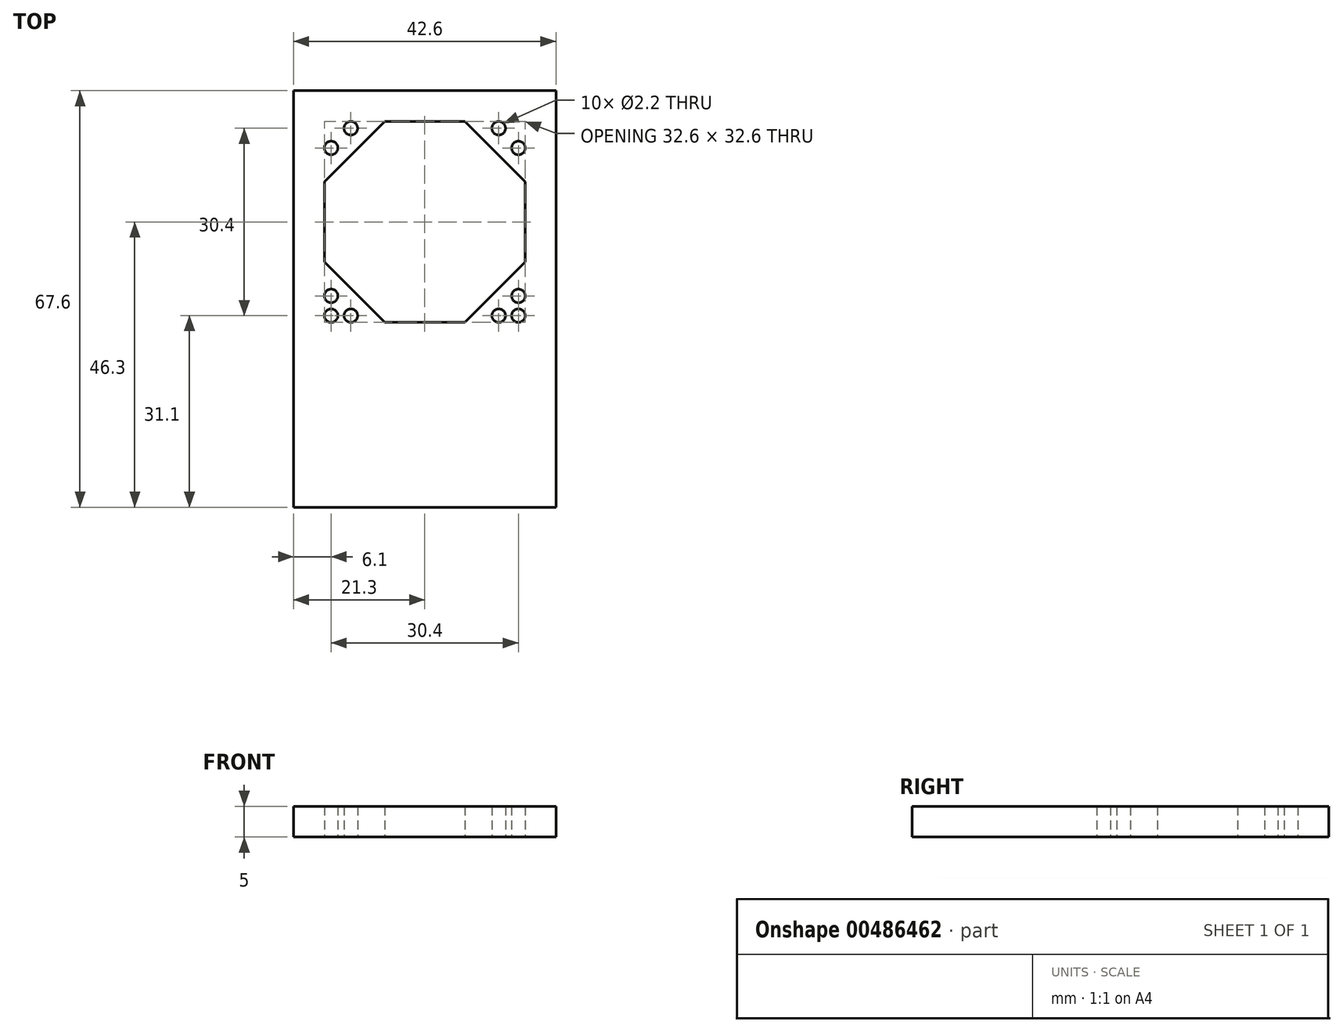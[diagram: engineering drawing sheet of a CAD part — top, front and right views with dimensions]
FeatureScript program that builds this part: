
annotation { "Feature Type Name" : "Feature", "Feature Type Description" : "" }
export const myFeature = defineFeature(function(context is Context, id is Id, definition is map)
    precondition{}
    {
        {
            var Q0;
            Q0=qCreatedBy(makeId("Top.planeOp"),FACE);
            var sketch = newSketch(context, id + "F0", { "sketchPlane" : qUnion([Q0])});
            skCircle(sketch, "E0", {"center": v(-12, 15.2) * mm, "radius": 1.1 * mm, "construction": true});
            skCircle(sketch, "E1", {"center": v(-15.2, 12) * mm, "radius": 1.1 * mm, "construction": true});
            skCircle(sketch, "E2.MirrorC", {"center": v(15.2, 12) * mm, "radius": 1.1 * mm, "construction": true});
            skCircle(sketch, "E3.MirrorC", {"center": v(12, 15.2) * mm, "radius": 1.1 * mm, "construction": true});
            skCircle(sketch, "E4.MirrorC", {"center": v(-12, -15.2) * mm, "radius": 1.1 * mm, "construction": true});
            skCircle(sketch, "E5.MirrorC", {"center": v(-15.2, -12) * mm, "radius": 1.1 * mm, "construction": true});
            skCircle(sketch, "E6.MirrorC", {"center": v(12, -15.2) * mm, "radius": 1.1 * mm, "construction": true});
            skCircle(sketch, "E7.MirrorC", {"center": v(15.2, -12) * mm, "radius": 1.1 * mm, "construction": true});
            skCircle(sketch, "E8", {"center": v(-15.2, -15.2) * mm, "radius": 1.1 * mm, "construction": true});
            skCircle(sketch, "E9.MirrorC", {"center": v(15.2, -15.2) * mm, "radius": 1.1 * mm, "construction": true});
            skArc(sketch, "E10", {"start": v(-14.1, -12) * mm, "mid": v(-15.2, -10.9) * mm, "end": v(-16.3, -12) * mm});
            skArc(sketch, "E11", {"start": v(-16.3, -15.2) * mm, "mid": v(-15.98, -15.98) * mm, "end": v(-15.2, -16.3) * mm});
            skArc(sketch, "E12", {"start": v(-12, -16.3) * mm, "mid": v(-10.9, -15.2) * mm, "end": v(-12, -14.1) * mm});
            skArc(sketch, "E13.MirrorCS", {"start": v(14.1, -12) * mm, "mid": v(15.2, -10.9) * mm, "end": v(16.3, -12) * mm});
            skArc(sketch, "E14.MirrorCS", {"start": v(16.3, -15.2) * mm, "mid": v(15.98, -15.98) * mm, "end": v(15.2, -16.3) * mm});
            skArc(sketch, "E15.MirrorCS", {"start": v(12, -16.3) * mm, "mid": v(10.9, -15.2) * mm, "end": v(12, -14.1) * mm});
            skLineSegment(sketch, "E16", {"start": v(-6.52, 16.3) * mm, "end": v(-16.3, 6.52) * mm});
            skLineSegment(sketch, "E17", {"start": v(-15.2, 12) * mm, "end": v(-12, 15.2) * mm, "construction": true});
            skLineSegment(sketch, "E18", {"start": v(-16.3, 6.52) * mm, "end": v(-16.3, 0) * mm});
            skLineSegment(sketch, "E19", {"start": v(-6.52, 16.3) * mm, "end": v(0, 16.3) * mm});
            skLineSegment(sketch, "E20.MirrorCS", {"start": v(6.52, 16.3) * mm, "end": v(0, 16.3) * mm});
            skLineSegment(sketch, "E21.MirrorCS", {"start": v(6.52, 16.3) * mm, "end": v(16.3, 6.52) * mm});
            skLineSegment(sketch, "E22.MirrorCS", {"start": v(16.3, 6.52) * mm, "end": v(16.3, 0) * mm});
            skLineSegment(sketch, "E23.MirrorCS", {"start": v(16.3, -6.52) * mm, "end": v(16.3, 0) * mm});
            skLineSegment(sketch, "E24.MirrorCS", {"start": v(6.52, -16.3) * mm, "end": v(16.3, -6.52) * mm});
            skLineSegment(sketch, "E25.MirrorCS", {"start": v(6.52, -16.3) * mm, "end": v(0, -16.3) * mm});
            skLineSegment(sketch, "E26.MirrorCS", {"start": v(-6.52, -16.3) * mm, "end": v(0, -16.3) * mm});
            skLineSegment(sketch, "E27.MirrorCS", {"start": v(-6.52, -16.3) * mm, "end": v(-16.3, -6.52) * mm});
            skLineSegment(sketch, "E28.MirrorCS", {"start": v(-16.3, -6.52) * mm, "end": v(-16.3, 0) * mm});
            skCircle(sketch, "E29", {"center": v(-15.2, 12) * mm, "radius": 1.1 * mm});
            skCircle(sketch, "E30", {"center": v(-12, 15.2) * mm, "radius": 1.1 * mm});
            skCircle(sketch, "E31.MirrorC", {"center": v(12, 15.2) * mm, "radius": 1.1 * mm});
            skCircle(sketch, "E32.MirrorC", {"center": v(15.2, 12) * mm, "radius": 1.1 * mm});
            skLineSegment(sketch, "E33.bottom", {"start": v(-21.3, 21.3) * mm, "end": v(21.3, 21.3) * mm});
            skLineSegment(sketch, "E33.top", {"start": v(-21.3, -46.3) * mm, "end": v(21.3, -46.3) * mm});
            skLineSegment(sketch, "E33.left", {"start": v(-21.3, 21.3) * mm, "end": v(-21.3, -46.3) * mm});
            skLineSegment(sketch, "E33.right", {"start": v(21.3, 21.3) * mm, "end": v(21.3, -46.3) * mm});
            skCircle(sketch, "E34", {"center": v(-15.2, -12) * mm, "radius": 1.1 * mm});
            skCircle(sketch, "E35", {"center": v(-15.2, -15.2) * mm, "radius": 1.1 * mm});
            skCircle(sketch, "E36", {"center": v(-12, -15.2) * mm, "radius": 1.1 * mm});
            skCircle(sketch, "E37", {"center": v(12, -15.2) * mm, "radius": 1.1 * mm});
            skCircle(sketch, "E38", {"center": v(15.2, -15.2) * mm, "radius": 1.1 * mm});
            skCircle(sketch, "E39", {"center": v(15.2, -12) * mm, "radius": 1.1 * mm});
            skSolve(sketch);
        }
        {
            var Q0;
            Q0=qSketchRegion(id+"F0",true);
            extrude(context, id + "F1", {"entities" : qUnion([Q0]), "depth" : 5 * mm});
        }
    });
